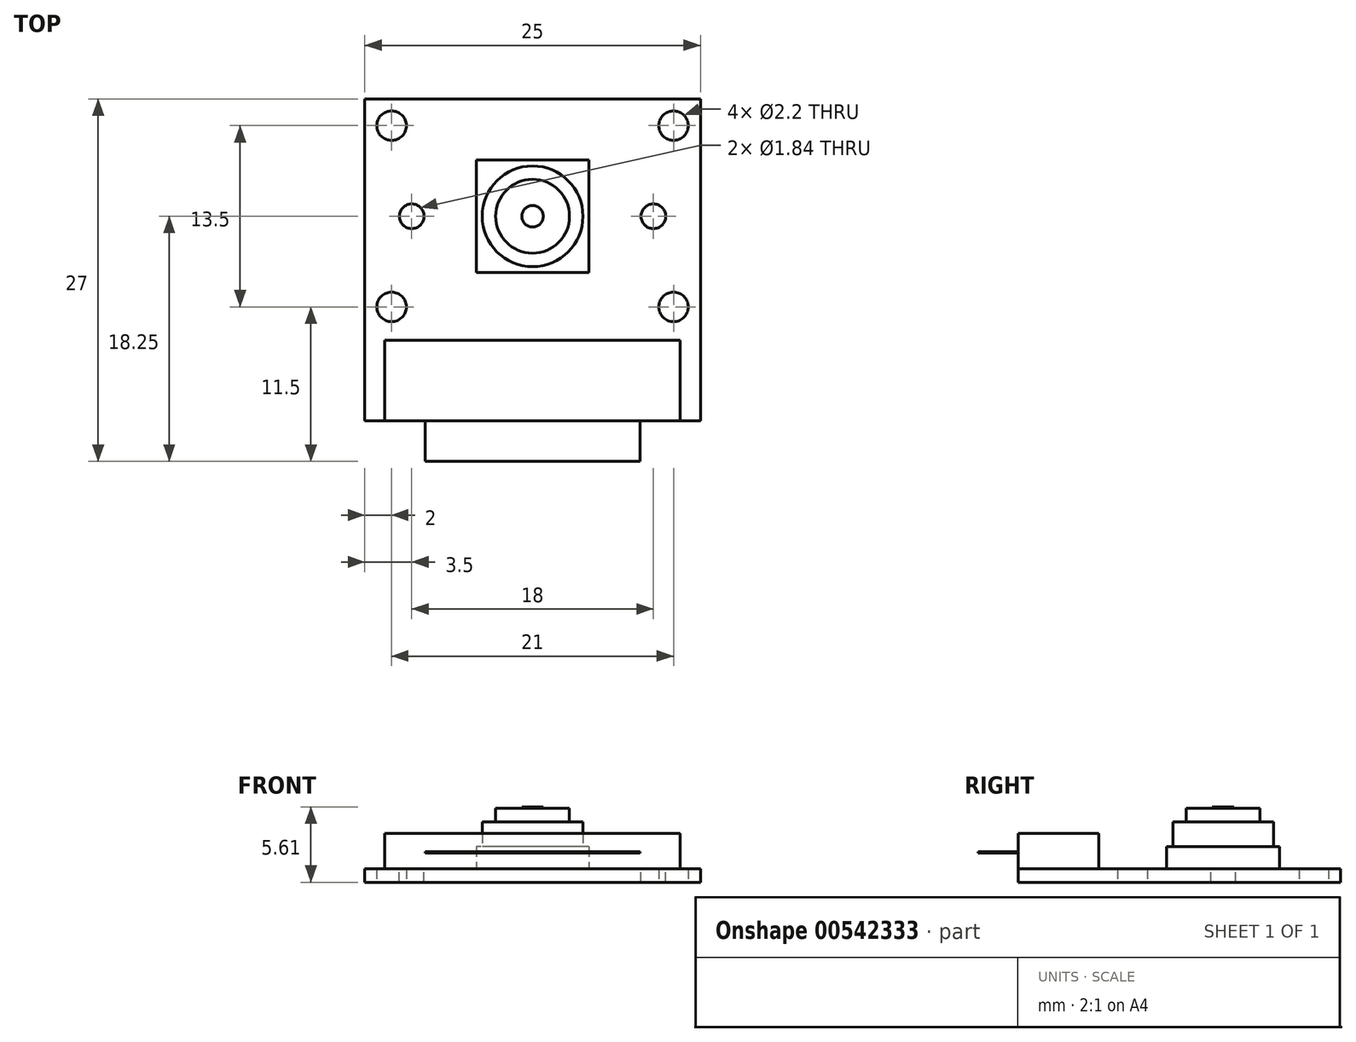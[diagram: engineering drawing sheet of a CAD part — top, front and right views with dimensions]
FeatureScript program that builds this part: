
annotation { "Feature Type Name" : "Feature", "Feature Type Description" : "" }
export const myFeature = defineFeature(function(context is Context, id is Id, definition is map)
    precondition{}
    {
        {
            var Q0;
            Q0=qCreatedBy(makeId("Top.planeOp"),FACE);
            var sketch = newSketch(context, id + "F0", { "sketchPlane" : qUnion([Q0])});
            skLineSegment(sketch, "E0.rect.bottom", {"start": v(12.5, 12) * mm, "end": v(-12.5, 12) * mm});
            skLineSegment(sketch, "E0.rect.top", {"start": v(12.5, -12) * mm, "end": v(-12.5, -12) * mm});
            skLineSegment(sketch, "E0.rect.left", {"start": v(12.5, 12) * mm, "end": v(12.5, -12) * mm});
            skLineSegment(sketch, "E0.rect.right", {"start": v(-12.5, 12) * mm, "end": v(-12.5, -12) * mm});
            skPoint(sketch, "E0.rect.middle", {"position": v(0, 0) * mm});
            skCircle(sketch, "E1", {"center": v(-10.5, 10) * mm, "radius": 1.1 * mm});
            skCircle(sketch, "E2", {"center": v(-10.5, -3.5) * mm, "radius": 1.1 * mm});
            skLineSegment(sketch, "E3", {"start": v(-10.5, 10) * mm, "end": v(-10.5, -12) * mm, "construction": true});
            skCircle(sketch, "E4.MirrorC", {"center": v(10.5, 10) * mm, "radius": 1.1 * mm});
            skCircle(sketch, "E5.MirrorC", {"center": v(10.5, -3.5) * mm, "radius": 1.1 * mm});
            skSolve(sketch);
        }
        {
            var Q0;
            Q0=makeQuery(id+"F0.imprint","IMPRINT",FACE,{"disambiguationData":[TD([[makeQuery(id+"F0.imprint","IMPRINT",EDGE,{"derivedFrom":sQuery(id+"F0.wireOp",EDGE,"E0.rect.bottom")}),1.0]])]});
            extrude(context, id + "F1", {"entities" : qUnion([Q0]), "depth" : 1 * mm});
        }
        {
            var Q0;
            Q0=makeQuery(id+"F1.opExtrude","CAP_FACE",FACE,{"disambiguationData":[OSD([sQuery(id+"F0.wireOp",EDGE,"E0.rect.bottom"),sQuery(id+"F0.wireOp",EDGE,"E0.rect.top"),sQuery(id+"F0.wireOp",EDGE,"E0.rect.left"),sQuery(id+"F0.wireOp",EDGE,"E0.rect.right"),sQuery(id+"F0.wireOp",EDGE,"E1"),sQuery(id+"F0.wireOp",EDGE,"E2"),sQuery(id+"F0.wireOp",EDGE,"E4.MirrorC"),sQuery(id+"F0.wireOp",EDGE,"E5.MirrorC")])],"isStart":false});
            var sketch = newSketch(context, id + "F2", { "sketchPlane" : qUnion([Q0])});
            skLineSegment(sketch, "E6", {"start": v(-12.5, 3.25) * mm, "end": v(12.5, 3.25) * mm, "construction": true});
            skLineSegment(sketch, "E7.rect.bottom", {"start": v(4.2, 7.45) * mm, "end": v(-4.2, 7.45) * mm});
            skLineSegment(sketch, "E7.rect.top", {"start": v(4.2, -0.95) * mm, "end": v(-4.2, -0.95) * mm});
            skLineSegment(sketch, "E7.rect.left", {"start": v(4.2, 7.45) * mm, "end": v(4.2, -0.95) * mm});
            skLineSegment(sketch, "E7.rect.right", {"start": v(-4.2, 7.45) * mm, "end": v(-4.2, -0.95) * mm});
            skPoint(sketch, "E7.rect.middle", {"position": v(0, 3.25) * mm});
            skCircle(sketch, "E8", {"center": v(0, 3.25) * mm, "radius": 3.75 * mm});
            skCircle(sketch, "E9", {"center": v(0, 3.25) * mm, "radius": 2.75 * mm});
            skLineSegment(sketch, "E10", {"start": v(-10.5, 10) * mm, "end": v(10.5, 10) * mm, "construction": true});
            skLineSegment(sketch, "E11", {"start": v(-10.5, -3.5) * mm, "end": v(10.5, -3.5) * mm, "construction": true});
            skCircle(sketch, "E12", {"center": v(-9, 3.25) * mm, "radius": 0.92 * mm});
            skCircle(sketch, "E13", {"center": v(9, 3.25) * mm, "radius": 0.92 * mm});
            skLineSegment(sketch, "E14", {"start": v(0, 10) * mm, "end": v(0, -3.5) * mm, "construction": true});
            skSolve(sketch);
        }
        {
            var Q0;
            Q0=makeQuery(id+"F2.imprint","IMPRINT",FACE,{"disambiguationData":[TD([[makeQuery(id+"F2.imprint","IMPRINT",EDGE,{"derivedFrom":sQuery(id+"F2.wireOp",EDGE,"E12")}),1.0]])]});
            var Q1;
            Q1=makeQuery(id+"F2.imprint","IMPRINT",FACE,{"disambiguationData":[TD([[makeQuery(id+"F2.imprint","IMPRINT",EDGE,{"derivedFrom":sQuery(id+"F2.wireOp",EDGE,"E13")}),1.0]])]});
            extrude(context, id + "F3", {"entities" : qUnion([Q0, Q1]), "operationType" : NewBodyOperationType.REMOVE, "endBound" : BoundingType.UP_TO_NEXT, "oppositeDirection" : true, "depth" : 25 * mm});
        }
        {
            var Q0;
            Q0=makeQuery(id+"F2.imprint","IMPRINT",FACE,{"disambiguationData":[TD([[makeQuery(id+"F2.imprint","IMPRINT",EDGE,{"derivedFrom":sQuery(id+"F2.wireOp",EDGE,"E7.rect.bottom")}),1.0]])]});
            var Q1;
            Q1=makeQuery(id+"F2.imprint","IMPRINT",FACE,{"disambiguationData":[TD([[makeQuery(id+"F2.imprint","IMPRINT",EDGE,{"derivedFrom":sQuery(id+"F2.wireOp",EDGE,"E8")}),1.0]])]});
            var Q2;
            Q2=makeQuery(id+"F2.imprint","IMPRINT",FACE,{"disambiguationData":[TD([[makeQuery(id+"F2.imprint","IMPRINT",EDGE,{"derivedFrom":sQuery(id+"F2.wireOp",EDGE,"E9")}),1.0]])]});
            extrude(context, id + "F4", {"entities" : qUnion([Q0, Q1, Q2]), "depth" : 1.65 * mm});
        }
        {
            var Q0;
            Q0=makeQuery(id+"F2.imprint","IMPRINT",FACE,{"disambiguationData":[TD([[makeQuery(id+"F2.imprint","IMPRINT",EDGE,{"derivedFrom":sQuery(id+"F2.wireOp",EDGE,"E8")}),1.0]])]});
            var Q1;
            Q1=makeQuery(id+"F2.imprint","IMPRINT",FACE,{"disambiguationData":[TD([[makeQuery(id+"F2.imprint","IMPRINT",EDGE,{"derivedFrom":sQuery(id+"F2.wireOp",EDGE,"E9")}),1.0]])]});
            extrude(context, id + "F5", {"entities" : qUnion([Q0, Q1]), "operationType" : NewBodyOperationType.ADD, "depth" : (1.65 + 1.86) * mm});
        }
        {
            var Q0;
            Q0=makeQuery(id+"F2.imprint","IMPRINT",FACE,{"disambiguationData":[TD([[makeQuery(id+"F2.imprint","IMPRINT",EDGE,{"derivedFrom":sQuery(id+"F2.wireOp",EDGE,"E9")}),1.0]])]});
            extrude(context, id + "F6", {"entities" : qUnion([Q0]), "operationType" : NewBodyOperationType.ADD, "depth" : (1.65 + 1.86 + 1) * mm});
        }
        {
            var Q0;
            Q0=makeQuery(id+"F6.opExtrude","CAP_FACE",FACE,{"disambiguationData":[OSD([sQuery(id+"F2.wireOp",EDGE,"E9")])],"isStart":false});
            var sketch = newSketch(context, id + "F7", { "sketchPlane" : qUnion([Q0])});
            skCircle(sketch, "E15", {"center": v(0, 3.25) * mm, "radius": 0.8 * mm});
            skSolve(sketch);
        }
        {
            var Q0;
            Q0=makeQuery(id+"F7.imprint","IMPRINT",FACE,{"disambiguationData":[TD([[makeQuery(id+"F7.imprint","IMPRINT",EDGE,{"derivedFrom":sQuery(id+"F7.wireOp",EDGE,"E15")}),1.0]])]});
            extrude(context, id + "F8", {"entities" : qUnion([Q0]), "depth" : 0.1 * mm});
        }
        {
            var Q0;
            Q0=makeQuery(id+"F2.imprint","IMPRINT",FACE,{"disambiguationData":[TD([[makeQuery(id+"F2.imprint","IMPRINT",EDGE,{"derivedFrom":sQuery(id+"F2.wireOp",EDGE,"E7.rect.bottom")}),-1.0]])]});
            var sketch = newSketch(context, id + "F9", { "sketchPlane" : qUnion([Q0])});
            skLineSegment(sketch, "E16.bottom", {"start": v(-11, -6) * mm, "end": v(11, -6) * mm});
            skLineSegment(sketch, "E16.top", {"start": v(-11, -12) * mm, "end": v(11, -12) * mm});
            skLineSegment(sketch, "E16.left", {"start": v(-11, -6) * mm, "end": v(-11, -12) * mm});
            skLineSegment(sketch, "E16.right", {"start": v(11, -6) * mm, "end": v(11, -12) * mm});
            skSolve(sketch);
        }
        {
            var Q0;
            Q0=qSketchRegion(id+"F9",true);
            extrude(context, id + "F10", {"entities" : qUnion([Q0]), "depth" : 2.65 * mm});
        }
        {
            var Q0;
            Q0=makeQuery(id+"F1.opExtrude","CAP_FACE",FACE,{"disambiguationData":[OSD([sQuery(id+"F0.wireOp",EDGE,"E0.rect.bottom"),sQuery(id+"F0.wireOp",EDGE,"E0.rect.top"),sQuery(id+"F0.wireOp",EDGE,"E0.rect.left"),sQuery(id+"F0.wireOp",EDGE,"E0.rect.right"),sQuery(id+"F0.wireOp",EDGE,"E1"),sQuery(id+"F0.wireOp",EDGE,"E2"),sQuery(id+"F0.wireOp",EDGE,"E4.MirrorC"),sQuery(id+"F0.wireOp",EDGE,"E5.MirrorC")])],"isStart":true});
            cPlane(context, id + "F11", {"entities" : qUnion([Q0]), "cplaneType" : CPlaneType.OFFSET, "offset" : (2.65 / 2 + 0.95) * mm, "oppositeDirection" : true, "width" : 150 * mm, "height" : 150 * mm});
        }
        {
            var Q0;
            Q0=qCreatedBy(id+"F11.planeOp",FACE);
            var sketch = newSketch(context, id + "F12", { "sketchPlane" : qUnion([Q0])});
            skLineSegment(sketch, "E17.bottom", {"start": v(-8, 12) * mm, "end": v(8, 12) * mm});
            skLineSegment(sketch, "E17.top", {"start": v(-8, 15) * mm, "end": v(8, 15) * mm});
            skLineSegment(sketch, "E17.left", {"start": v(-8, 12) * mm, "end": v(-8, 15) * mm});
            skLineSegment(sketch, "E17.right", {"start": v(8, 12) * mm, "end": v(8, 15) * mm});
            skSolve(sketch);
        }
        {
            var Q0;
            Q0=makeQuery(id+"F12.imprint","IMPRINT",FACE,{"disambiguationData":[TD([[makeQuery(id+"F12.imprint","IMPRINT",EDGE,{"derivedFrom":sQuery(id+"F12.wireOp",EDGE,"E17.bottom")}),1.0]])]});
            extrude(context, id + "F13", {"entities" : qUnion([Q0]), "depth" : 0.1 * mm});
        }
    });
